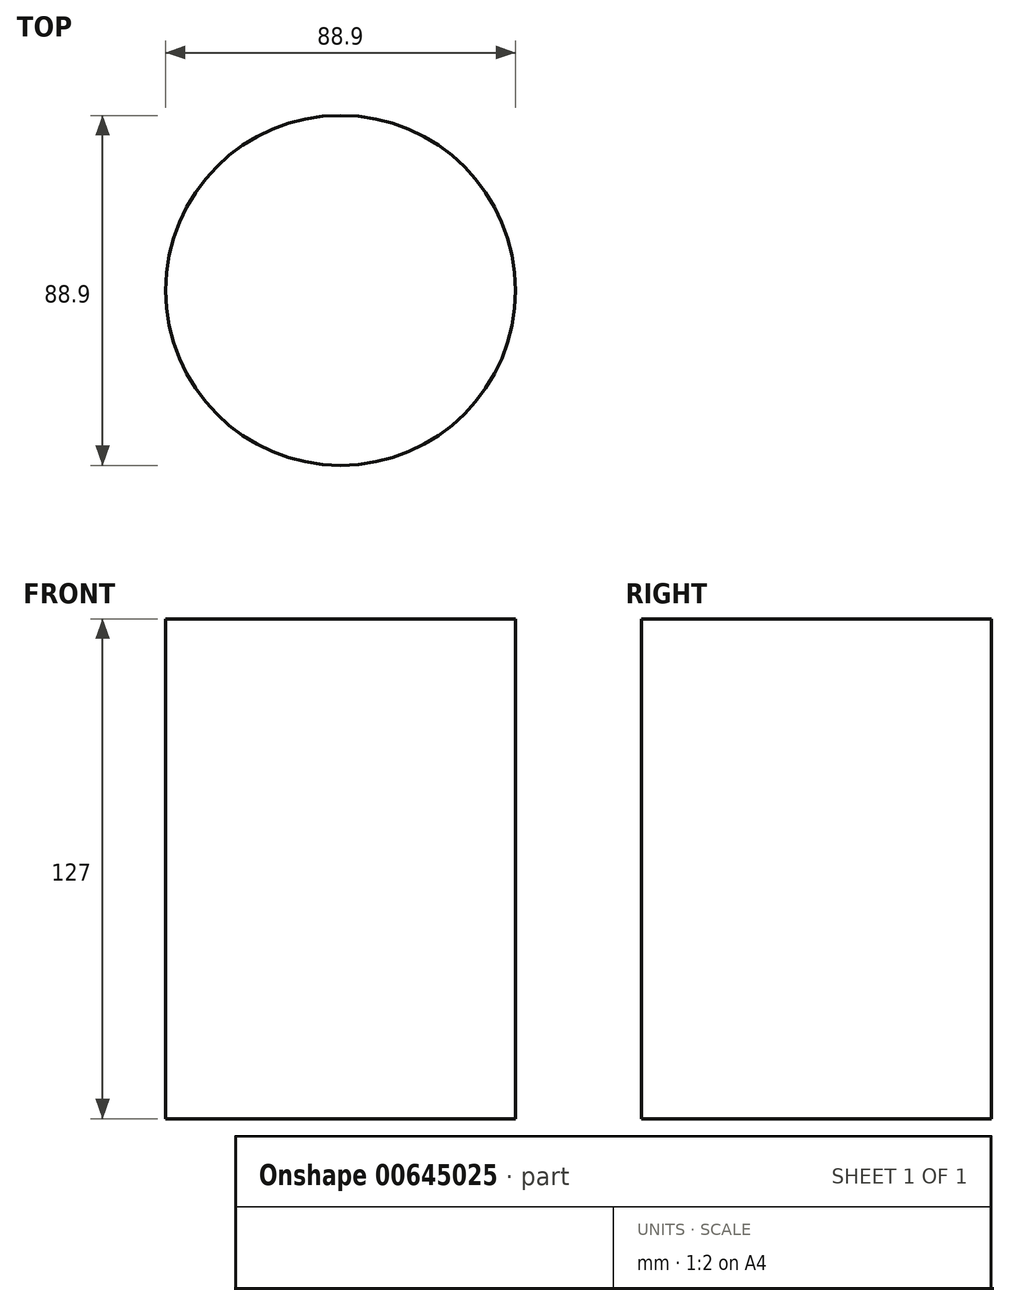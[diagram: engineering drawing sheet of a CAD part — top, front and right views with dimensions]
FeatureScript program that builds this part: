
annotation { "Feature Type Name" : "Feature", "Feature Type Description" : "" }
export const myFeature = defineFeature(function(context is Context, id is Id, definition is map)
    precondition{}
    {
        {
            var Q0;
            Q0=qCreatedBy(makeId("Top.planeOp"),FACE);
            var sketch = newSketch(context, id + "F0", { "sketchPlane" : qUnion([Q0])});
            skCircle(sketch, "E0", {"center": v(0, 0) * mm, "radius": 44.45 * mm});
            skSolve(sketch);
        }
        {
            var Q0;
            Q0=makeQuery(id+"F0.imprint","IMPRINT",FACE,{"disambiguationData":[TD([[makeQuery(id+"F0.imprint","IMPRINT",EDGE,{"derivedFrom":sQuery(id+"F0.wireOp",EDGE,"E0")}),1.0]])]});
            extrude(context, id + "F1", {"entities" : qUnion([Q0]), "endBound" : BoundingType.SYMMETRIC, "depth" : 127 * mm, "offsetDistance" : 25.4 * mm});
        }
    });
